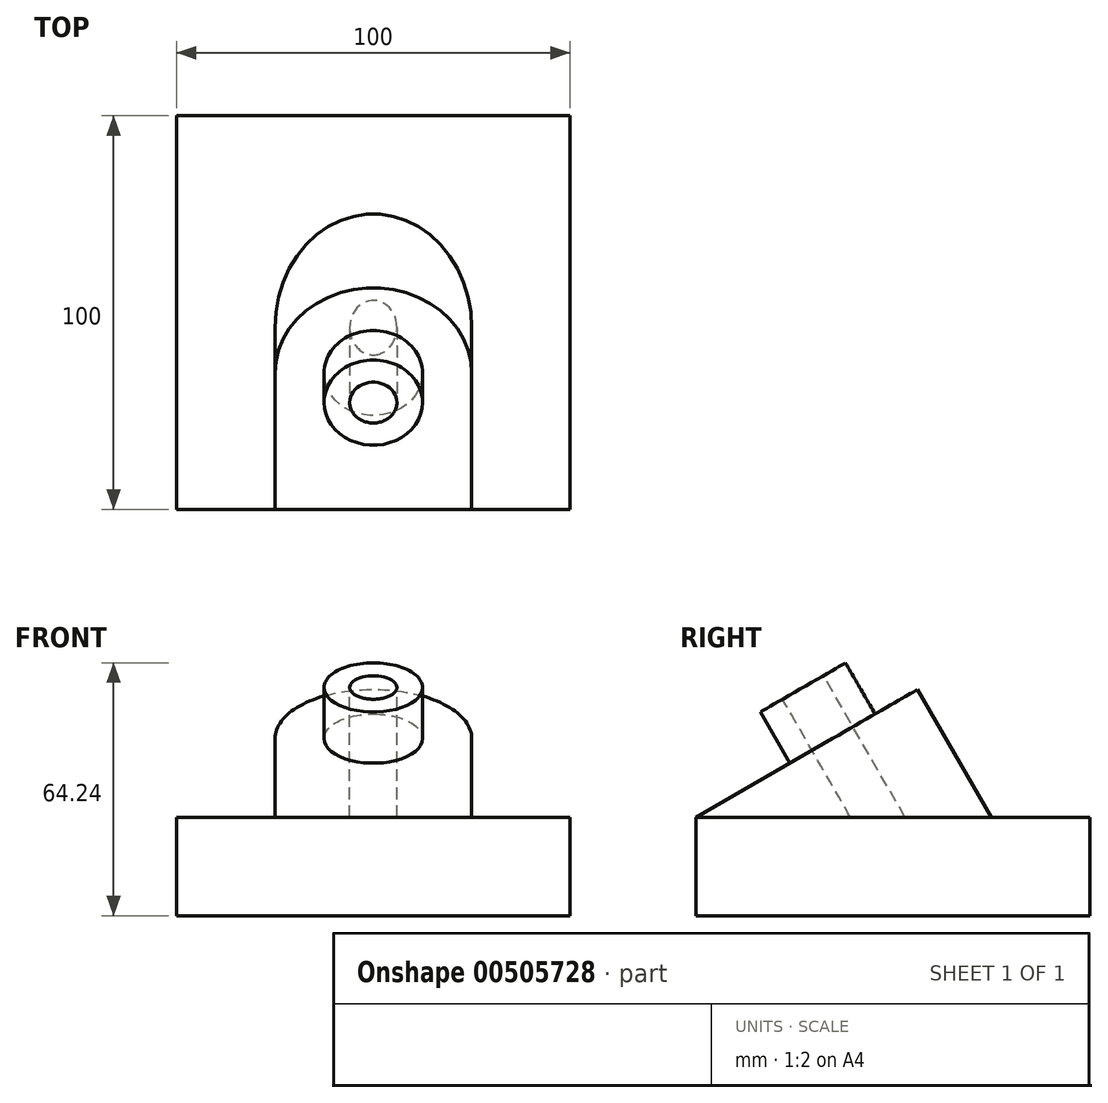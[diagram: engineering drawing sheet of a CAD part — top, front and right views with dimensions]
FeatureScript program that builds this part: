
annotation { "Feature Type Name" : "Feature", "Feature Type Description" : "" }
export const myFeature = defineFeature(function(context is Context, id is Id, definition is map)
    precondition{}
    {
        {
            var Q0;
            Q0=qCreatedBy(makeId("Top.planeOp"),FACE);
            var sketch = newSketch(context, id + "F0", { "sketchPlane" : qUnion([Q0])});
            skLineSegment(sketch, "E0.bottom", {"start": v(-50, 0) * mm, "end": v(50, 0) * mm});
            skLineSegment(sketch, "E0.top", {"start": v(-50, 100) * mm, "end": v(50, 100) * mm});
            skLineSegment(sketch, "E0.left", {"start": v(-50, 0) * mm, "end": v(-50, 100) * mm});
            skLineSegment(sketch, "E0.right", {"start": v(50, 0) * mm, "end": v(50, 100) * mm});
            skPoint(sketch, "E1", {"position": v(0, 0) * mm});
            skSolve(sketch);
        }
        {
            var Q0;
            Q0 = qSketchRegion(id + "F0", true);
            extrude(context, id + "F1", {"entities" : qUnion([Q0]), "depth" : 25 * mm});
        }
        {
            var Q0;
            Q0=makeQuery(id+"F1.opExtrude","CAP_FACE",FACE,{"disambiguationData":[OSD([sQuery(id+"F0.wireOp",EDGE,"E0.bottom"),sQuery(id+"F0.wireOp",EDGE,"E0.top"),sQuery(id+"F0.wireOp",EDGE,"E0.left"),sQuery(id+"F0.wireOp",EDGE,"E0.right")])],"isStart":false});
            var Q1;
            Q1=makeQuery(id+"F1.opExtrude","CAP_EDGE",EDGE,{"disambiguationData":[OSD([sQuery(id+"F0.wireOp",EDGE,"E0.bottom")])],"isStart":false});
            cPlane(context, id + "F2", {"entities" : qUnion([Q0, Q1]), "cplaneType" : CPlaneType.LINE_ANGLE, "offset" : 25 * mm, "angle" : 30 * degree, "width" : 150 * mm, "height" : 150 * mm});
        }
        {
            var Q0;
            Q0=qCreatedBy(id+"F2.planeOp",FACE);
            var sketch = newSketch(context, id + "F3", { "sketchPlane" : qUnion([Q0])});
            skLineSegment(sketch, "E2.bottom", {"start": v(-25, -52.5) * mm, "end": v(25, -52.5) * mm});
            skLineSegment(sketch, "E2.top", {"start": v(-25, -12.5) * mm, "end": v(25, -12.5) * mm});
            skLineSegment(sketch, "E2.left", {"start": v(-25, -52.5) * mm, "end": v(-25, -12.5) * mm});
            skLineSegment(sketch, "E2.right", {"start": v(25, -52.5) * mm, "end": v(25, -12.5) * mm});
            skPoint(sketch, "E3", {"position": v(0, -12.5) * mm});
            skArc(sketch, "E4", {"start": v(-25, -52.5) * mm, "mid": v(0, -77.5) * mm, "end": v(25, -52.5) * mm});
            skSolve(sketch);
        }
        {
            var Q0;
            Q0 = qSketchRegion(id + "F3", true);
            extrude(context, id + "F4", {"entities" : qUnion([Q0]), "operationType" : NewBodyOperationType.ADD, "endBound" : BoundingType.UP_TO_NEXT, "depth" : 25 * mm});
        }
        {
            var Q0;
            Q0=makeQuery(id+"F3.imprint","IMPRINT",FACE,{"disambiguationData":[TD([[makeQuery(id+"F3.imprint","IMPRINT",EDGE,{"derivedFrom":sQuery(id+"F3.wireOp",EDGE,"E2.bottom")}),-1.0]])]});
            var sketch = newSketch(context, id + "F5", { "sketchPlane" : qUnion([Q0])});
            skCircle(sketch, "E5", {"center": v(0, -52.5) * mm, "radius": 12.5 * mm});
            skSolve(sketch);
        }
        {
            var Q0;
            Q0 = qSketchRegion(id + "F5", true);
            extrude(context, id + "F6", {"entities" : qUnion([Q0]), "operationType" : NewBodyOperationType.ADD, "oppositeDirection" : true, "depth" : 15 * mm});
        }
        {
            var Q0;
            Q0=makeQuery(id+"F6.opExtrude","CAP_FACE",FACE,{"disambiguationData":[OSD([sQuery(id+"F5.wireOp",EDGE,"E5")])],"isStart":false});
            var sketch = newSketch(context, id + "F7", { "sketchPlane" : qUnion([Q0])});
            skCircle(sketch, "E6", {"center": v(0, 52.5) * mm, "radius": 6 * mm});
            skSolve(sketch);
        }
        {
            var Q0;
            Q0 = qSketchRegion(id + "F7", true);
            var Q1;
            Q1=makeQuery(id+"F1.opExtrude","CAP_FACE",FACE,{"disambiguationData":[OSD([sQuery(id+"F0.wireOp",EDGE,"E0.bottom"),sQuery(id+"F0.wireOp",EDGE,"E0.top"),sQuery(id+"F0.wireOp",EDGE,"E0.left"),sQuery(id+"F0.wireOp",EDGE,"E0.right")])],"isStart":false});
            extrude(context, id + "F8", {"entities" : qUnion([Q0]), "operationType" : NewBodyOperationType.REMOVE, "endBound" : BoundingType.UP_TO_SURFACE, "oppositeDirection" : true, "endBoundEntityFace" : qUnion([Q1]), "depth" : 25 * mm});
        }
    });
